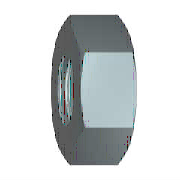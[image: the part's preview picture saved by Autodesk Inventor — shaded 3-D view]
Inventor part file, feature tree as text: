
AUTODESK INVENTOR PART (.ipt)
format: ipt  version: 2020 (Build 240168000, 168)  size: 165,888 bytes
history: native  units: mm (DEFAULTED — no unit token found)
features: sketch x3, other x2, extrude x1, hole x1, plane x1
ambient origin geometry x7: Origin, YZ Plane, XZ Plane, X Axis, Y Axis, Z Axis, Center Point
bodies: Solid1 (feature_tree)
feature tree (8):
  extrude  "Bryła"  Depth=4.618802mm
  other  "Faza1"
  hole  "Gwint"  [1 undecoded]
  other  "Work Axis1"
  plane  "Work Plane1"
  sketch  "Szkic1"
  sketch  "Szkic2"
  sketch  "Szkic3"
note: 1 required parameter value undecoded (feature->parameter linkage not recoverable at this tier; creation-order binding heuristic only, values carry confidence <= 0.55)
